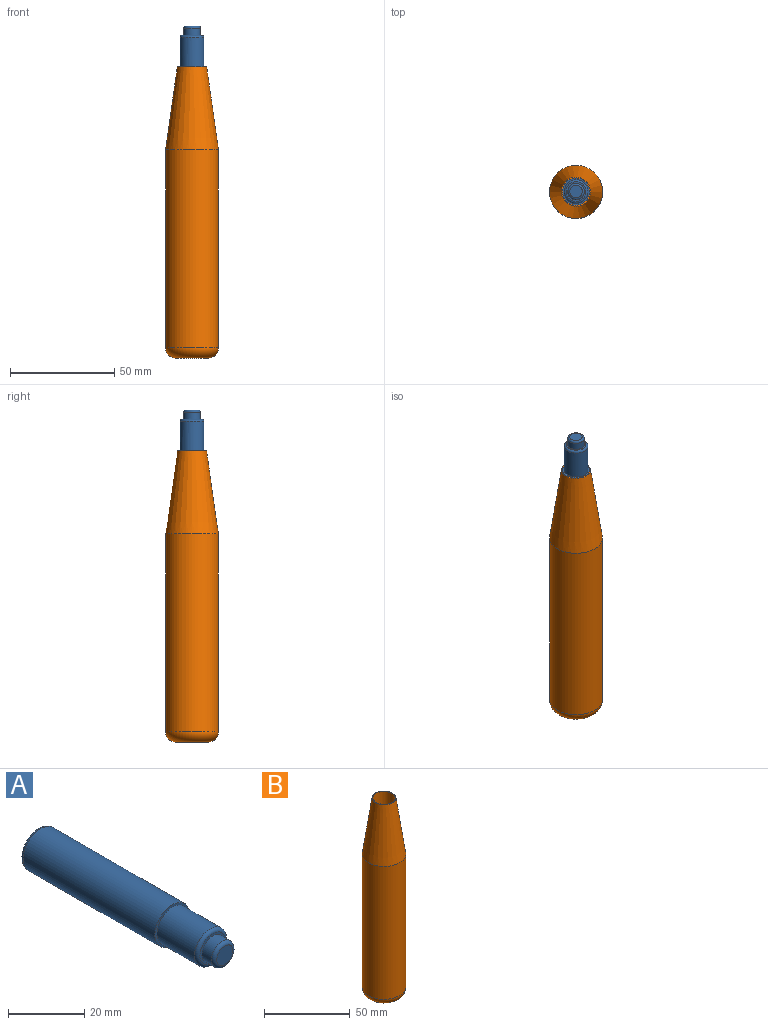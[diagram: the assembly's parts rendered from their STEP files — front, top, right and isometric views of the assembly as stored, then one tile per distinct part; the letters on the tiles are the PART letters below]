
ASSEMBLY  parts=2 mates=1
PART A: 10 faces, bbox 14.1x69.5x14.1 mm
  f0: cylinder r=6.5mm len=49mm, axis (0,1,0), area 2001.2mm2, adj f1,f9
  f1: plane 13x13mm, normal (0,-1,0), area 28.9mm2, adj f0,f3
  f2: plane 11x11mm, normal (0,1,0), area 95mm2, adj f9
  f3: cylinder r=5.75mm len=14mm, axis (0,1,0), area 505.8mm2, adj f1,f8
  f4: plane 9.5x9.5mm, normal (0,-1,0), area 20.6mm2, adj f5,f8
  f5: cylinder r=4mm len=8mm, axis (0,1,0), area 88mm2, adj f4,f7
  f6: plane 6x6mm, normal (0,-1,0), area 28.3mm2, adj f7
  f7: torus R=3mm, axis (0,-1,0), area 35.9mm2, adj f5,f6
  f8: torus R=4.75mm, axis (0,-1,0), area 53.2mm2, adj f3,f4
  f9: torus R=5.5mm, axis (0,-1,0), area 60.6mm2, adj f0,f2
PART B: 7 faces, bbox 27.5x27.5x140 mm
  f0: cone r=12.7mm half-angle=8.1deg, axis (0,0,-1), area 2500.6mm2, adj f1,f3
  f1: cylinder r=12.7mm len=95mm, axis (0,0,-1), area 7580.7mm2, adj f0,f6
  f2: plane 15.4x15.4mm, normal (0,0,-1), area 186.3mm2, adj f6
  f3: plane 14x14mm, normal (0,0,1), area 21.2mm2, adj f0,f4
  f4: cylinder r=6.5mm len=50mm, axis (0,0,1), area 2042mm2, adj f3,f5
  f5: cone r=0mm half-angle=59deg, axis (0,0,1), area 154.8mm2, adj f4
  f6: torus R=7.7mm, axis (0,0,-1), area 537.1mm2, adj f1,f2
PLACE A rot(axis=(-1,0,0),90deg) t=(0,0,44.21)mm
PLACE B at identity
MATE cylindrical A.f0 <-> B.f0  axis (0,0,1) through (0,0,94.21)mm
